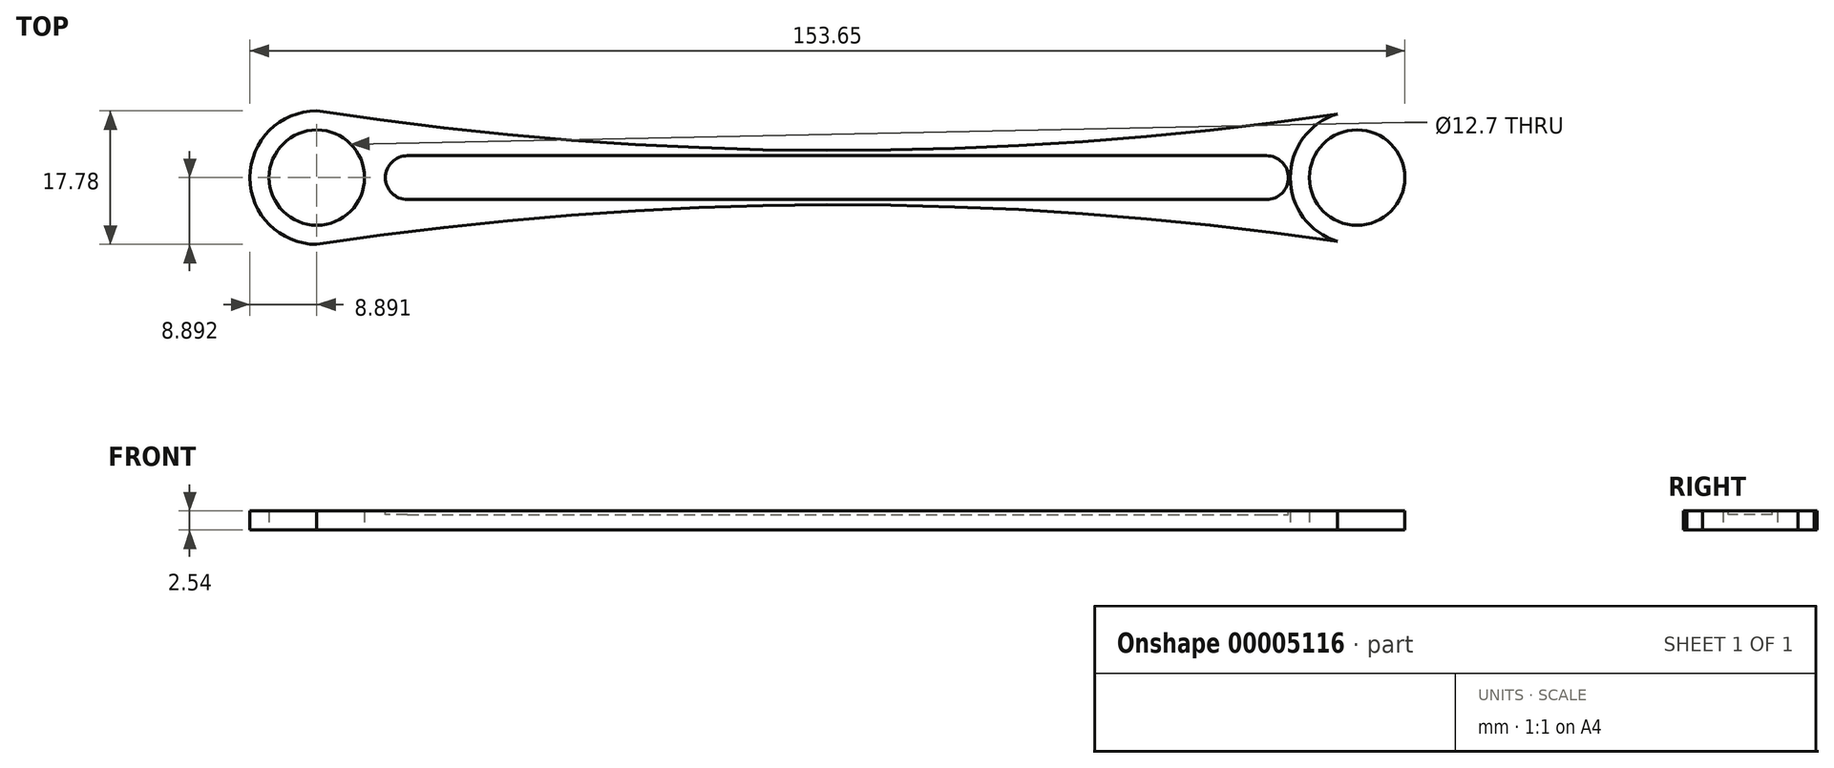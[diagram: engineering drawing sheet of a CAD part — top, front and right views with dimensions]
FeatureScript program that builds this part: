
annotation { "Feature Type Name" : "Feature", "Feature Type Description" : "" }
export const myFeature = defineFeature(function(context is Context, id is Id, definition is map)
    precondition{}
    {
        {
            var Q0;
            Q0=qCreatedBy(makeId("Top.planeOp"),FACE);
            var sketch = newSketch(context, id + "F0", { "sketchPlane" : qUnion([Q0])});
            skCircle(sketch, "E0", {"center": v(-76.82, 3.52) * mm, "radius": 6.35 * mm});
            skLineSegment(sketch, "E1", {"start": v(-7.62, 21.16) * mm, "end": v(-7.62, -25.07) * mm, "construction": true});
            skCircle(sketch, "E2.0.MirrorC", {"center": v(61.59, 3.52) * mm, "radius": 6.35 * mm});
            skCircle(sketch, "E3.0", {"center": v(-76.82, 3.52) * mm, "radius": 8.9 * mm});
            skCircle(sketch, "E4.0.MirrorC", {"center": v(61.59, 3.52) * mm, "radius": 8.9 * mm});
            skLineSegment(sketch, "E5", {"start": v(-76.82, 3.52) * mm, "end": v(61.59, 3.52) * mm, "construction": true});
            skArc(sketch, "E6", {"start": v(61.59, -5.37) * mm, "mid": v(-7.62, -0.1) * mm, "end": v(-76.82, -5.37) * mm});
            skArc(sketch, "E7.0.MirrorCS", {"start": v(61.59, 12.41) * mm, "mid": v(-7.62, 7.14) * mm, "end": v(-76.82, 12.41) * mm});
            skPoint(sketch, "E8.rect.middle", {"position": v(-7.62, 3.52) * mm});
            skSolve(sketch);
        }
        {
            var Q0;
            Q0=makeQuery(id+"F0.imprint","IMPRINT",FACE,{"disambiguationData":[TD([[makeQuery(id+"F0.imprint","IMPRINT",EDGE,{"derivedFrom":sQuery(id+"F0.wireOp",EDGE,"E0")}),-1.0]])]});
            var Q1;
            {var subQ0=sQuery(id+"F0.wireOp",EDGE,"E7.0.MirrorCS");var subQ3=sQuery(id+"F0.wireOp",EDGE,"E3.0");var subQ4=makeQuery(id+"F0.imprint","INTERSECT",VERTEX,{"disambiguationData":[OD(1.0)],"derivedFrom":[subQ3,subQ0]});Q1=makeQuery(id+"F0.imprint","IMPRINT",FACE,{"disambiguationData":[TD([[makeQuery(id+"F0.imprint","IMPRINT",EDGE,{"disambiguationData":[TD([[subQ4,1.0]])],"derivedFrom":subQ3}),-1.0]])]});}
            var Q2;
            Q2=makeQuery(id+"F0.imprint","IMPRINT",FACE,{"disambiguationData":[TD([[makeQuery(id+"F0.imprint","IMPRINT",EDGE,{"derivedFrom":sQuery(id+"F0.wireOp",EDGE,"E2.0.MirrorC")}),1.0]])]});
            extrude(context, id + "F1", {"entities" : qUnion([Q0, Q1, Q2]), "depth" : 2.54 * mm});
        }
        {
            var Q0;
            Q0=makeQuery(id+"F1.opExtrude","CAP_FACE",FACE,{"disambiguationData":[OSD([sQuery(id+"F0.wireOp",EDGE,"E0"),sQuery(id+"F0.wireOp",EDGE,"E2.0.MirrorC"),sQuery(id+"F0.wireOp",EDGE,"E3.0"),sQuery(id+"F0.wireOp",EDGE,"E4.0.MirrorC"),sQuery(id+"F0.wireOp",EDGE,"E6"),sQuery(id+"F0.wireOp",EDGE,"E7.0.MirrorCS")])],"isStart":false});
            var sketch = newSketch(context, id + "F2", { "sketchPlane" : qUnion([Q0])});
            skCircle(sketch, "E9.0", {"center": v(-76.82, 3.52) * mm, "radius": 6.35 * mm, "construction": true});
            skCircle(sketch, "E10.0", {"center": v(61.59, 3.52) * mm, "radius": 6.35 * mm, "construction": true});
            skLineSegment(sketch, "E11", {"start": v(-76.82, 3.52) * mm, "end": v(61.59, 3.52) * mm, "construction": true});
            skLineSegment(sketch, "E12", {"start": v(-7.62, 3.52) * mm, "end": v(-7.62, 23.23) * mm, "construction": true});
            skLineSegment(sketch, "E13.rect.bottom", {"start": v(-64.77, 0.6) * mm, "end": v(49.53, 0.6) * mm});
            skLineSegment(sketch, "E13.rect.top", {"start": v(-64.77, 6.44) * mm, "end": v(49.53, 6.44) * mm});
            skLineSegment(sketch, "E13.rect.left", {"start": v(-64.77, 0.6) * mm, "end": v(-64.77, 6.44) * mm});
            skLineSegment(sketch, "E13.rect.right", {"start": v(49.53, 0.6) * mm, "end": v(49.53, 6.44) * mm});
            skPoint(sketch, "E13.rect.middle", {"position": v(-7.62, 3.52) * mm});
            skCircle(sketch, "E14", {"center": v(-64.77, 3.52) * mm, "radius": 2.92 * mm});
            skCircle(sketch, "E15.0.MirrorC", {"center": v(49.53, 3.52) * mm, "radius": 2.92 * mm});
            skSolve(sketch);
        }
        {
            var Q0;
            {var subQ3=sQuery(id+"F2.wireOp",EDGE,"E13.rect.bottom");var subQ5=sQuery(id+"F2.wireOp",EDGE,"E14");var subQ7=makeQuery(id+"F2.imprint","INTERSECT",VERTEX,{"derivedFrom":[subQ3,subQ5]});Q0=makeQuery(id+"F2.imprint","IMPRINT",FACE,{"disambiguationData":[TD([[makeQuery(id+"F2.imprint","IMPRINT",EDGE,{"disambiguationData":[TD([[subQ7,-1.0]])],"derivedFrom":subQ3}),1.0]])]});}
            var Q1;
            {var subQ5=sQuery(id+"F2.wireOp",EDGE,"E13.rect.right");Q1=makeQuery(id+"F2.imprint","IMPRINT",FACE,{"disambiguationData":[TD([[makeQuery(id+"F2.imprint","IMPRINT",EDGE,{"derivedFrom":subQ5}),-1.0]])]});}
            var Q2;
            {var subQ5=sQuery(id+"F2.wireOp",EDGE,"E13.rect.left");Q2=makeQuery(id+"F2.imprint","IMPRINT",FACE,{"disambiguationData":[TD([[makeQuery(id+"F2.imprint","IMPRINT",EDGE,{"derivedFrom":subQ5}),1.0]])]});}
            var Q3;
            {var subQ5=sQuery(id+"F2.wireOp",EDGE,"E13.rect.left");Q3=makeQuery(id+"F2.imprint","IMPRINT",FACE,{"disambiguationData":[TD([[makeQuery(id+"F2.imprint","IMPRINT",EDGE,{"derivedFrom":subQ5}),-1.0]])]});}
            var Q4;
            {var subQ5=sQuery(id+"F2.wireOp",EDGE,"E13.rect.right");Q4=makeQuery(id+"F2.imprint","IMPRINT",FACE,{"disambiguationData":[TD([[makeQuery(id+"F2.imprint","IMPRINT",EDGE,{"derivedFrom":subQ5}),1.0]])]});}
            extrude(context, id + "F3", {"entities" : qUnion([Q0, Q1, Q2, Q3, Q4]), "operationType" : NewBodyOperationType.REMOVE, "oppositeDirection" : true, "depth" : 0.5 * mm});
        }
    });
